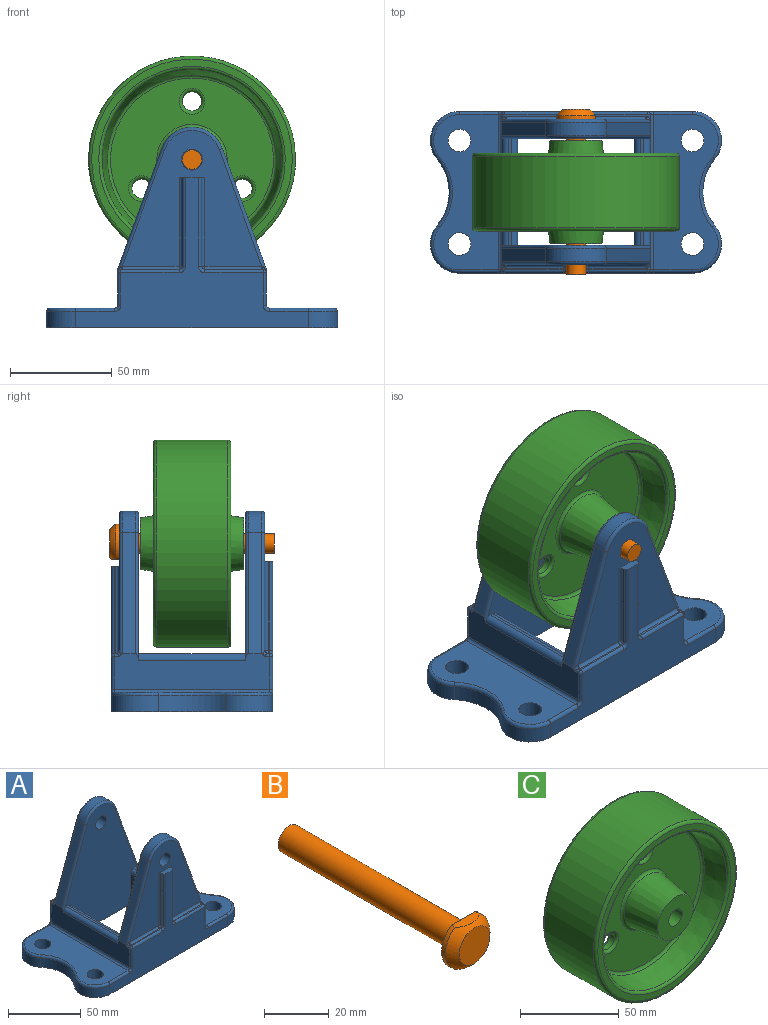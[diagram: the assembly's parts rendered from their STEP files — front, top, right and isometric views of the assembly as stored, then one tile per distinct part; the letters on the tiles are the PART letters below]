
ASSEMBLY  parts=3 mates=3
PART A: 117 faces, bbox 146.6x83.1x101.1 mm
  f0: plane 68.49x66.68mm, normal (0,-1,0), area 2276.1mm2, adj f34,f40,f69,f70,f71,f97,f100,f107
  f1: plane 96.84x69.99mm, normal (0,-1,0), area 4578mm2, adj f8,f9,f20,f21,f28,f42,f63,f64
  f2: plane 96.84x69.99mm, normal (0,1,0), area 4578mm2, adj f8,f9,f20,f21,f28,f40,f66,f67
  f3: plane 77.54x18.81mm, normal (1,0,0), area 1151.7mm2, adj f39,f41,f56,f60,f62,f65,f68,f71
  f4: plane 68.49x66.68mm, normal (0,1,0), area 2306.3mm2, adj f31,f42,f72,f73,f74,f83,f84,f87
  f5: plane 77.54x18.81mm, normal (-1,0,0), area 1151.7mm2, adj f36,f37,f44,f49,f52,f63,f66,f69
  f6: plane 28.58x0.86mm, normal (0,0,1), area 22.7mm2, adj f91,f93,f100,f101,f110
  f7: plane 30.16x0.86mm, normal (0,0,1), area 24mm2, adj f29,f76,f78,f84,f85
  f8: plane 52.39x1.59mm, normal (0,0,1), area 83.2mm2, adj f1,f2,f105,f106
  f9: plane 52.39x1.59mm, normal (0,0,1), area 83.2mm2, adj f1,f2,f103,f104
  f10: plane 30.16x0.86mm, normal (0,0,1), area 24mm2, adj f30,f80,f82,f88,f89
  f11: plane 28.58x0.86mm, normal (0,0,1), area 22.7mm2, adj f94,f96,f97,f98,f114
  f12: plane 76.2x31.75mm, normal (0,0,1), area 1891.8mm2, adj f23,f24,f53,f54,f55,f57,f59,f60
  f13: plane 114.3x73.82mm, normal (0,-1,0), area 2543.9mm2, adj f14,f22,f28,f34,f44,f45,f47,f55
  f14: cylinder r=14.29mm len=23.43mm, axis (0,0,-1), area 256.9mm2, adj f13,f15,f28,f53
  f15: cylinder r=25.4mm len=32.51mm, axis (0,0,-1), area 280mm2, adj f14,f16,f28,f54
  f16: cylinder r=14.29mm len=23.43mm, axis (0,0,-1), area 256.9mm2, adj f15,f17,f28,f57
  f17: plane 114.3x71.44mm, normal (0,1,0), area 2524.5mm2, adj f16,f18,f28,f31,f50,f51,f52,f59
  f18: cylinder r=14.29mm len=23.43mm, axis (0,0,-1), area 256.9mm2, adj f17,f19,f28,f48
  f19: cylinder r=25.4mm len=32.51mm, axis (0,0,-1), area 280mm2, adj f18,f22,f28,f46
  f20: plane 52.39x25.4mm, normal (1,0,0), area 1330.6mm2, adj f1,f2,f28,f106
  f21: plane 52.39x25.4mm, normal (-1,0,0), area 1330.6mm2, adj f1,f2,f28,f104
  f22: cylinder r=14.29mm len=23.43mm, axis (0,0,-1), area 256.9mm2, adj f13,f19,f28,f43
  f23: cylinder r=5.56mm len=11.11mm, axis (0,0,-1), area 332.5mm2, adj f12,f28
  f24: cylinder r=5.56mm len=11.11mm, axis (0,0,-1), area 332.5mm2, adj f12,f28
  f25: cylinder r=5.56mm len=11.11mm, axis (0,0,-1), area 332.5mm2, adj f27,f28
  f26: cylinder r=5.56mm len=11.11mm, axis (0,0,-1), area 332.5mm2, adj f27,f28
  f27: plane 76.2x31.75mm, normal (0,0,1), area 1891.8mm2, adj f25,f26,f43,f45,f46,f48,f49,f50
  f28: plane 142.88x79.38mm, normal (0,0,-1), area 7268.5mm2, adj f1,f2,f13,f14,f15,f16,f17,f18
  f29: plane 42.86x0.79mm, normal (-1,0,0), area 34mm2, adj f7,f31,f75,f83
  f30: plane 42.86x0.79mm, normal (1,0,0), area 34mm2, adj f10,f31,f79,f87
  f31: plane 12.7x3.97mm, normal (0,0,1), area 37.8mm2, adj f4,f17,f29,f30,f75,f79,f83,f87
  f32: plane 43.66x0.79mm, normal (1,0,0), area 34.7mm2, adj f34,f107,f109,f110
  f33: plane 43.66x0.79mm, normal (-1,0,0), area 34.7mm2, adj f34,f112,f114,f115
  f34: plane 12.7x3.97mm, normal (0,0,1), area 37.8mm2, adj f0,f13,f32,f33,f107,f109,f112,f115
  f35: cylinder r=15.88mm len=29.84mm, axis (0,-1,0), area 246.4mm2, adj f36,f39,f67,f70
  f36: plane 59.4x21.59mm, normal (-0.94,0,0.34), area 401.3mm2, adj f5,f35,f66,f69
  f37: plane 59.4x21.59mm, normal (-0.94,0,0.34), area 401.3mm2, adj f5,f38,f63,f72
  f38: cylinder r=15.88mm len=29.84mm, axis (0,-1,0), area 246.4mm2, adj f37,f41,f64,f73
  f39: plane 59.4x21.59mm, normal (0.94,0,0.34), area 401.3mm2, adj f3,f35,f68,f71
  f40: cylinder r=5.16mm len=10.32mm, axis (0,-1,0), area 308.8mm2, adj f0,f2
  f41: plane 59.4x21.59mm, normal (0.94,0,0.34), area 401.3mm2, adj f3,f38,f65,f74
  f42: cylinder r=5.16mm len=10.32mm, axis (0,-1,0), area 308.8mm2, adj f1,f4
  f43: torus R=12.7mm, axis (0,0,1), area 77.4mm2, adj f22,f27,f45,f46
  f44: cylinder r=1.59mm len=15.88mm, axis (0,0,1), area 39.6mm2, adj f5,f13,f47,f95
  f45: cylinder r=1.59mm len=19.05mm, axis (-1,0,0), area 47.5mm2, adj f13,f27,f43,f47
  f46: torus R=26.99mm, axis (0,0,1), area 90mm2, adj f19,f27,f43,f48
  f47: torus R=3.17mm, axis (0,-1,0), area 8.5mm2, adj f13,f44,f45,f49
  f48: torus R=12.7mm, axis (0,0,1), area 77.4mm2, adj f18,f27,f46,f50
  f49: cylinder r=1.59mm len=76.2mm, axis (0,-1,0), area 190mm2, adj f5,f27,f47,f51
  f50: cylinder r=1.59mm len=19.05mm, axis (1,0,0), area 47.5mm2, adj f17,f27,f48,f51
  f51: torus R=3.17mm, axis (0,1,0), area 8.5mm2, adj f17,f49,f50,f52
  f52: cylinder r=1.59mm len=15.88mm, axis (0,0,1), area 39.6mm2, adj f5,f17,f51,f77
  f53: torus R=12.7mm, axis (0,0,1), area 77.4mm2, adj f12,f14,f54,f55
  f54: torus R=26.99mm, axis (0,0,1), area 90mm2, adj f12,f15,f53,f57
  f55: cylinder r=1.59mm len=19.05mm, axis (-1,0,0), area 47.5mm2, adj f12,f13,f53,f58
  f56: cylinder r=1.59mm len=15.88mm, axis (0,0,-1), area 39.6mm2, adj f3,f13,f58,f92
  f57: torus R=12.7mm, axis (0,0,1), area 77.4mm2, adj f12,f16,f54,f59
  f58: torus R=3.17mm, axis (0,-1,0), area 8.5mm2, adj f13,f55,f56,f60
  f59: cylinder r=1.59mm len=19.05mm, axis (1,0,0), area 47.5mm2, adj f12,f17,f57,f61
  f60: cylinder r=1.59mm len=76.2mm, axis (0,1,0), area 190mm2, adj f3,f12,f58,f61
  f61: torus R=3.17mm, axis (0,1,0), area 8.5mm2, adj f17,f59,f60,f62
  f62: cylinder r=1.59mm len=15.88mm, axis (0,0,-1), area 39.6mm2, adj f3,f17,f61,f81
  f63: cylinder r=1.59mm len=62.75mm, axis (-0.34,0,-0.94), area 160.4mm2, adj f1,f5,f37,f64,f105
  f64: torus R=14.29mm, axis (0,1,0), area 93.2mm2, adj f1,f38,f63,f65
  f65: cylinder r=1.59mm len=62.75mm, axis (-0.34,0,0.94), area 160.4mm2, adj f1,f3,f41,f64,f103
  f66: cylinder r=1.59mm len=62.75mm, axis (0.34,0,0.94), area 160.4mm2, adj f2,f5,f36,f67,f105
  f67: torus R=14.29mm, axis (0,1,0), area 93.2mm2, adj f2,f35,f66,f68
  f68: cylinder r=1.59mm len=62.75mm, axis (0.34,0,-0.94), area 160.4mm2, adj f2,f3,f39,f67,f103
  f69: cylinder r=1.59mm len=60.54mm, axis (0.34,0,0.94), area 155.7mm2, adj f0,f5,f36,f70,f98,f99
  f70: torus R=14.29mm, axis (0,1,0), area 93.2mm2, adj f0,f35,f69,f71
  f71: cylinder r=1.59mm len=60.54mm, axis (0.34,0,-0.94), area 155.7mm2, adj f0,f3,f39,f70,f101,f102
  f72: cylinder r=1.59mm len=60.54mm, axis (-0.34,0,-0.94), area 155.7mm2, adj f4,f5,f37,f73,f85,f86
  f73: torus R=14.29mm, axis (0,1,0), area 93.2mm2, adj f4,f38,f72,f74
  f74: cylinder r=1.59mm len=60.54mm, axis (-0.34,0,0.94), area 155.7mm2, adj f3,f4,f41,f73,f89,f90
  f75: cylinder r=1.59mm len=44.45mm, axis (0,0,-1), area 108.9mm2, adj f17,f29,f31,f76
  f76: cylinder r=1.59mm len=31.75mm, axis (1,0,0), area 77.2mm2, adj f7,f17,f75,f77
  f77: sphere r=1.59mm, area 5.4mm2, adj f52,f76,f78
  f78: cylinder r=1.59mm len=2.35mm, axis (0,1,0), area 4.4mm2, adj f5,f7,f77,f86
  f79: cylinder r=1.59mm len=44.45mm, axis (0,0,1), area 108.9mm2, adj f17,f30,f31,f80
  f80: cylinder r=1.59mm len=31.75mm, axis (1,0,0), area 77.2mm2, adj f10,f17,f79,f81
  f81: sphere r=1.59mm, area 2.5mm2, adj f62,f80,f82
  f82: cylinder r=1.59mm len=2.35mm, axis (0,-1,0), area 4.4mm2, adj f3,f10,f81,f90
  f83: cylinder r=1.59mm len=42.86mm, axis (0,0,1), area 104.9mm2, adj f4,f29,f31,f84
  f84: cylinder r=1.59mm len=29.48mm, axis (-1,0,0), area 71.5mm2, adj f4,f7,f83,f85
  f85: bspline ~1.62x1.59mm, area 1.2mm2, adj f7,f72,f84,f86
  f86: bspline ~3.73x2.5mm, area 4.2mm2, adj f5,f72,f78,f85
  f87: cylinder r=1.59mm len=42.86mm, axis (0,0,-1), area 104.9mm2, adj f4,f30,f31,f88
  f88: cylinder r=1.59mm len=29.48mm, axis (-1,0,0), area 71.5mm2, adj f4,f10,f87,f89
  f89: bspline ~1.62x1.59mm, area 1.2mm2, adj f10,f74,f88,f90
  f90: bspline ~3.73x2.5mm, area 4.2mm2, adj f3,f74,f82,f89
  f91: cylinder r=1.59mm len=28.58mm, axis (-1,0,0), area 71.3mm2, adj f6,f13,f92,f111
  f92: sphere r=1.59mm, area 4mm2, adj f56,f91,f93
  f93: cylinder r=1.59mm len=2.35mm, axis (0,-1,0), area 4.4mm2, adj f3,f6,f92,f102
  f94: cylinder r=1.59mm len=28.58mm, axis (-1,0,0), area 71.3mm2, adj f11,f13,f95,f116
  f95: sphere r=1.59mm, area 4mm2, adj f44,f94,f96
  f96: cylinder r=1.59mm len=2.35mm, axis (0,1,0), area 4.4mm2, adj f5,f11,f95,f99
  f97: cylinder r=1.59mm len=27.9mm, axis (1,0,0), area 69.6mm2, adj f0,f11,f98,f113
  f98: bspline ~1.62x1.59mm, area 1.2mm2, adj f11,f69,f97,f99
  f99: bspline ~3.73x2.5mm, area 4.2mm2, adj f5,f69,f96,f98
  f100: cylinder r=1.59mm len=27.9mm, axis (1,0,0), area 69.6mm2, adj f0,f6,f101,f108
  f101: bspline ~1.62x1.59mm, area 1.2mm2, adj f6,f71,f100,f102
  f102: bspline ~3.73x2.5mm, area 4.2mm2, adj f3,f71,f93,f101
  f103: cylinder r=3.17mm len=52.55mm, axis (0,-1,0), area 261.5mm2, adj f1,f2,f3,f9,f65,f68
  f104: cylinder r=3.17mm len=52.39mm, axis (0,1,0), area 261.3mm2, adj f1,f2,f9,f21
  f105: cylinder r=3.17mm len=52.55mm, axis (0,1,0), area 261.5mm2, adj f1,f2,f5,f8,f63,f66
  f106: cylinder r=3.17mm len=52.39mm, axis (0,-1,0), area 261.3mm2, adj f1,f2,f8,f20
  f107: cylinder r=1.59mm len=43.66mm, axis (0,0,-1), area 108.9mm2, adj f0,f32,f34,f108
  f108: sphere r=1.59mm, area 4mm2, adj f100,f107,f110
  f109: cylinder r=1.59mm len=43.66mm, axis (0,0,-1), area 108.9mm2, adj f13,f32,f34,f111
  f110: cylinder r=1.59mm len=1.59mm, axis (0,1,0), area 2mm2, adj f6,f32,f108,f111
  f111: torus R=3.17mm, axis (0,-1,0), area 8.5mm2, adj f13,f91,f109,f110
  f112: cylinder r=1.59mm len=43.66mm, axis (0,0,1), area 108.9mm2, adj f0,f33,f34,f113
  f113: sphere r=1.59mm, area 4mm2, adj f97,f112,f114
  f114: cylinder r=1.59mm len=1.59mm, axis (0,-1,0), area 2mm2, adj f11,f33,f113,f116
  f115: cylinder r=1.59mm len=43.66mm, axis (0,0,1), area 108.9mm2, adj f13,f33,f34,f116
  f116: torus R=3.17mm, axis (0,-1,0), area 8.5mm2, adj f13,f94,f114,f115
PART B: 7 faces, bbox 19.1x81x19.1 mm
  f0: cylinder r=9.53mm len=19.05mm, axis (0,-1,0), area 77.3mm2, adj f1,f5,f6
  f1: sphere r=11.11mm, area 202.5mm2, adj f0,f2,f6
  f2: plane 13.31x13.31mm, normal (0,-1,0), area 139.2mm2, adj f1
  f3: plane 9.49x9.49mm, normal (0,1,0), area 70.7mm2, adj f4
  f4: cylinder r=4.74mm len=76.2mm, axis (0,-1,0), area 2271.1mm2, adj f3,f5
  f5: plane 19.05x17.46mm, normal (0,1,0), area 203mm2, adj f0,f4,f6
  f6: plane 10.53x3.64mm, normal (0,0,1), area 31.6mm2, adj f0,f1,f5
PART C: 29 faces, bbox 110x50.8x110 mm
  f0: torus R=45.75mm, axis (0,-1,0), area 614mm2, adj f1,f18
  f1: cone r=44.19mm half-angle=11.3deg, axis (0,-1,0), area 3659mm2, adj f0,f2
  f2: torus R=39.97mm, axis (0,-1,0), area 560.3mm2, adj f1,f3
  f3: plane 79.95x79.95mm, normal (0,-1,0), area 3704.9mm2, adj f2,f4,f22,f23,f24
  f4: torus R=17.25mm, axis (0,-1,0), area 232.3mm2, adj f3,f5
  f5: cone r=12.7mm half-angle=8.1deg, axis (0,1,0), area 1878.9mm2, adj f4,f6
  f6: plane 25.4x25.4mm, normal (0,-1,0), area 434.1mm2, adj f5,f28
  f7: plane 25.4x25.4mm, normal (0,1,0), area 434.1mm2, adj f8,f28
  f8: cone r=15.49mm half-angle=8.1deg, axis (0,-1,0), area 1744.1mm2, adj f7,f9
  f9: torus R=18.63mm, axis (0,-1,0), area 476.6mm2, adj f8,f10
  f10: plane 77.34x77.34mm, normal (0,1,0), area 3228.1mm2, adj f9,f11,f25,f26,f27
  f11: torus R=38.67mm, axis (0,-1,0), area 1110.5mm2, adj f10,f12
  f12: cone r=41.79mm half-angle=11.3deg, axis (0,1,0), area 3318.4mm2, adj f11,f13
  f13: torus R=45.75mm, axis (0,-1,0), area 614mm2, adj f12,f14
  f14: plane 98.43x98.43mm, normal (0,1,0), area 1032.6mm2, adj f13,f15
  f15: torus R=49.21mm, axis (0,-1,0), area 786.9mm2, adj f14,f16
  f16: cylinder r=50.8mm len=101.6mm, axis (0,-1,0), area 11147.6mm2, adj f15,f17
  f17: torus R=49.21mm, axis (0,-1,0), area 786.9mm2, adj f16,f18
  f18: plane 98.43x98.43mm, normal (0,-1,0), area 1032.6mm2, adj f0,f17
  f19: cylinder r=4.76mm len=9.53mm, axis (0,-1,0), area 95mm2, adj f22,f25
  f20: cylinder r=4.76mm len=9.53mm, axis (0,-1,0), area 95mm2, adj f23,f27
  f21: cylinder r=4.76mm len=9.53mm, axis (0,-1,0), area 95mm2, adj f24,f26
  f22: torus R=6.35mm, axis (0,1,0), area 83.7mm2, adj f3,f19
  f23: torus R=6.35mm, axis (0,1,0), area 83.7mm2, adj f3,f20
  f24: torus R=6.35mm, axis (0,1,0), area 83.7mm2, adj f3,f21
  f25: torus R=6.35mm, axis (0,-1,0), area 83.7mm2, adj f10,f19
  f26: torus R=6.35mm, axis (0,-1,0), area 83.7mm2, adj f10,f21
  f27: torus R=6.35mm, axis (0,-1,0), area 83.7mm2, adj f10,f20
  f28: cylinder r=4.81mm len=50.8mm, axis (0,-1,0), area 1534.3mm2, adj f6,f7
PLACE A t=(17.29,30.4,3.65)mm
PLACE B rot(axis=(1,0,0),180deg) t=(17.29,66.12,86.2)mm
PLACE C rot(axis=(0,1,0),0deg) t=(17.29,4.91,86.2)mm
MATE planar B.f0 <-> A.f4  axis (0,-1,0) through (17.29,66.12,86.2)mm
MATE cylindrical C.f0 <-> B.f0  axis (0,-1,0) through (17.29,30.31,86.2)mm
MATE cylindrical B.f0 <-> A.f35  axis (0,1,0) through (17.29,28.02,86.2)mm
